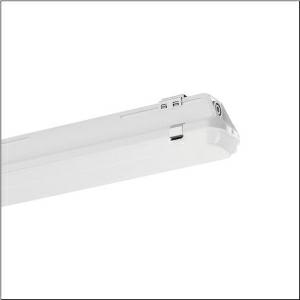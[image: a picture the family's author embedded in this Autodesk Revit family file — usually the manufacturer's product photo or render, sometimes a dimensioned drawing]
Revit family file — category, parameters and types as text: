
# Revit family: monsun_21_51fb207l440k005
name_source: partatom
category: Lighting Fixtures
units: mm (PartAtom-declared; Revit-internal decimal feet)

## family parameters
Cut with Voids When Loaded = No
Host = Face
Light Source = No
Part Type = Normal
Room Calculation Point = No
Round Connector Dimension = Use Diameter
Shared = No

## types (1)
- Monsun 21 (1 x LED, 4330 lm, 27.2 W, 4000K)
    Apparent Load = 27 VA
    CIE Flux Codes = 45 75 93 94 100
    Color Rendering = 80
    Color Temperature = 4000K
    Default Elevation = 1800 mm
    Description = Monsun 21, damp-proof luminaire, chain hanger, primary optical cover: enclosure, of PC, light emission: direct distribution, primary light characteristic: symmetric, installation type: vertical mounting, horizontal mounting, surface-mounted, suspended mounting, LED, rated luminous flux: 4.330lm, luminous efficacy: 159lm/W, light colour: 840, colour temperature: 4000K, control gear: ON/OFF, with terminal, 3-pole, max. 2.5mm², through-wiring: 5x 2.5mm², mains connection: 220..240V, AC, 50/60Hz, rated input power: 27W, housing, of glass-fibre reinforced plastic, uncoated, bright grey, incl. chain hanger, length: 1.299mm, width: 90mm, height: 88mm, clip for enclosure, of stainless steel (V2A), ceiling mounting element, of stainless steel (V2A), chain hanger, of stainless steel (V2A), protection rating (complete): IP66, insulation class (complete): insulation class I (protective earthing), certification: CE, ENEC, VDE, UKCA, protection symbol: D, impact resistance: IK08, permissible operating ambient temperature: -25..+35°C, standard: EN 50419, EN 60598-2-1, corresponds to IFS (International Featured Standards) requirements for safety and quality in the food industry, for indoor or canopied outdoor use, no direct snow, no direct sun, no direct rain, LABS conformity tested according to VDMA 24364:2018-05, contact your sales advisor before using the luminaires in applications with unclear chemical exposure, large temperature fluctuations or condensation-forming humidity, packaging unit: 1 piece
    Height = 88 mm
    Lamp = 1 x LED
    Lamp Light Flux = 4330 lm
    Lamp Power = 27.2 W
    Lamp count = 1
    Length = 1299 mm
    Luminous efficacy = 159 lm/W
    Manufacturer = Siteco
    ModVariant = No
    Model = 51FB207L440K005
    Mounting Place = Ceiling
    Mounting Type = Surface mounted
    Number of Poles = 1
    OnlyDefault = Yes
    Power Factor = 1
    Product Name = Monsun 21
    Product group = damp-proof luminaire
    ProductGroupID = 300
    Protection Class = Protection class I
    Protection Degree = IP 66
    RLX_Detail_Level = 1
    RLX_Emergency_Light_Flux = 0 lm
    RLX_Emergency_Type = 0
    RLX_Emergency_Type_DB = No
    RlxData = <blob elided: 89749 chars, md5=9cd54b38>
    Socket = socket
    Standby Power = 0 W
    System Light Flux = 4330 lm
    System Power = 27 W
    Type Comments = Product without accessories
    Type Image = l_1319656.jpg
    URL = http://relux.com
    VarID = ---
    Voltage = 0 V
    Weight = 0.00 kg
    Width = 90 mm

## geometry (parser evidence)
native form markers: Blend x4, Sweep x15
no freeform markers — native parametric forms only
